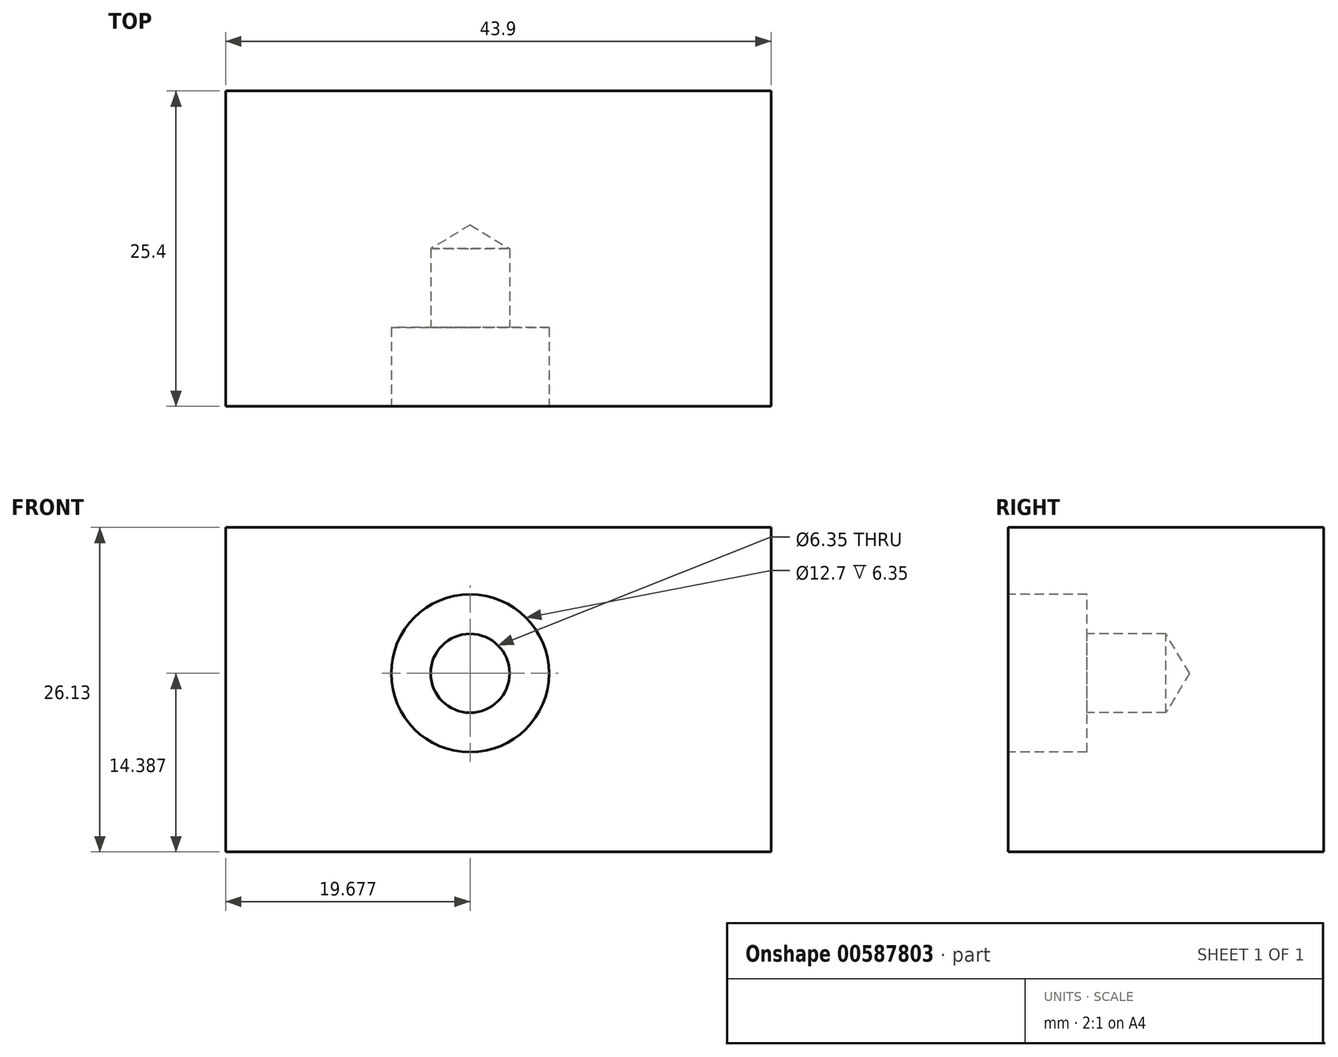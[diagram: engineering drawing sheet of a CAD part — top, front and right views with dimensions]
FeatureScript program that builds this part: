
annotation { "Feature Type Name" : "Feature", "Feature Type Description" : "" }
export const myFeature = defineFeature(function(context is Context, id is Id, definition is map)
    precondition{}
    {
        {
            var Q0;
            Q0=qCreatedBy(makeId("Front.planeOp"),FACE);
            var sketch = newSketch(context, id + "F0", { "sketchPlane" : qUnion([Q0])});
            skLineSegment(sketch, "E0.bottom", {"start": v(0, 0) * mm, "end": v(-43.9, 0) * mm});
            skLineSegment(sketch, "E0.top", {"start": v(0, 26.13) * mm, "end": v(-43.9, 26.13) * mm});
            skLineSegment(sketch, "E0.left", {"start": v(0, 0) * mm, "end": v(0, 26.13) * mm});
            skLineSegment(sketch, "E0.right", {"start": v(-43.9, 0) * mm, "end": v(-43.9, 26.13) * mm});
            skSolve(sketch);
        }
        {
            var Q0;
            Q0 = qSketchRegion(id + "F0", true);
            extrude(context, id + "F1", {"entities" : qUnion([Q0]), "depth" : 25.4 * mm, "offsetDistance" : 25.4 * mm});
        }
        {
            var Q0;
            Q0=makeQuery(id+"F1.opExtrude","CAP_FACE",FACE,{"disambiguationData":[OSD([sQuery(id+"F0.wireOp",EDGE,"E0.bottom"),sQuery(id+"F0.wireOp",EDGE,"E0.top"),sQuery(id+"F0.wireOp",EDGE,"E0.left"),sQuery(id+"F0.wireOp",EDGE,"E0.right")])],"isStart":false});
            var sketch = newSketch(context, id + "F2", { "sketchPlane" : qUnion([Q0])});
            skPoint(sketch, "E1", {"position": v(-24.22, 14.39) * mm});
            skSolve(sketch);
        }
        {
            var Q0;
            Q0=sQuery(id+"F2.wireOp",VERTEX,"E1");
            var Q1;
            Q1=makeQuery(id+"F1.opExtrude","SWEPT_BODY",BODY,{"disambiguationData":[OSD([sQuery(id+"F0.wireOp",EDGE,"E0.bottom"),sQuery(id+"F0.wireOp",EDGE,"E0.top"),sQuery(id+"F0.wireOp",EDGE,"E0.left"),sQuery(id+"F0.wireOp",EDGE,"E0.right")])]});
            hole(context, id + "F3", {"style" : HoleStyle.C_BORE, "endStyle" : HoleEndStyle.BLIND, "holeDiameter" : 6.35 * mm, "cBoreDiameter" : 12.7 * mm, "cBoreDepth" : 6.35 * mm, "majorDiameter" : 6.35 * mm, "holeDepth" : 12.7 * mm, "isTappedThrough" : true, "tappedDepth" : 12.7 * mm, "tapClearance" : 3, "locations" : qUnion([Q0]), "scope" : qUnion([Q1])});
        }
    });
